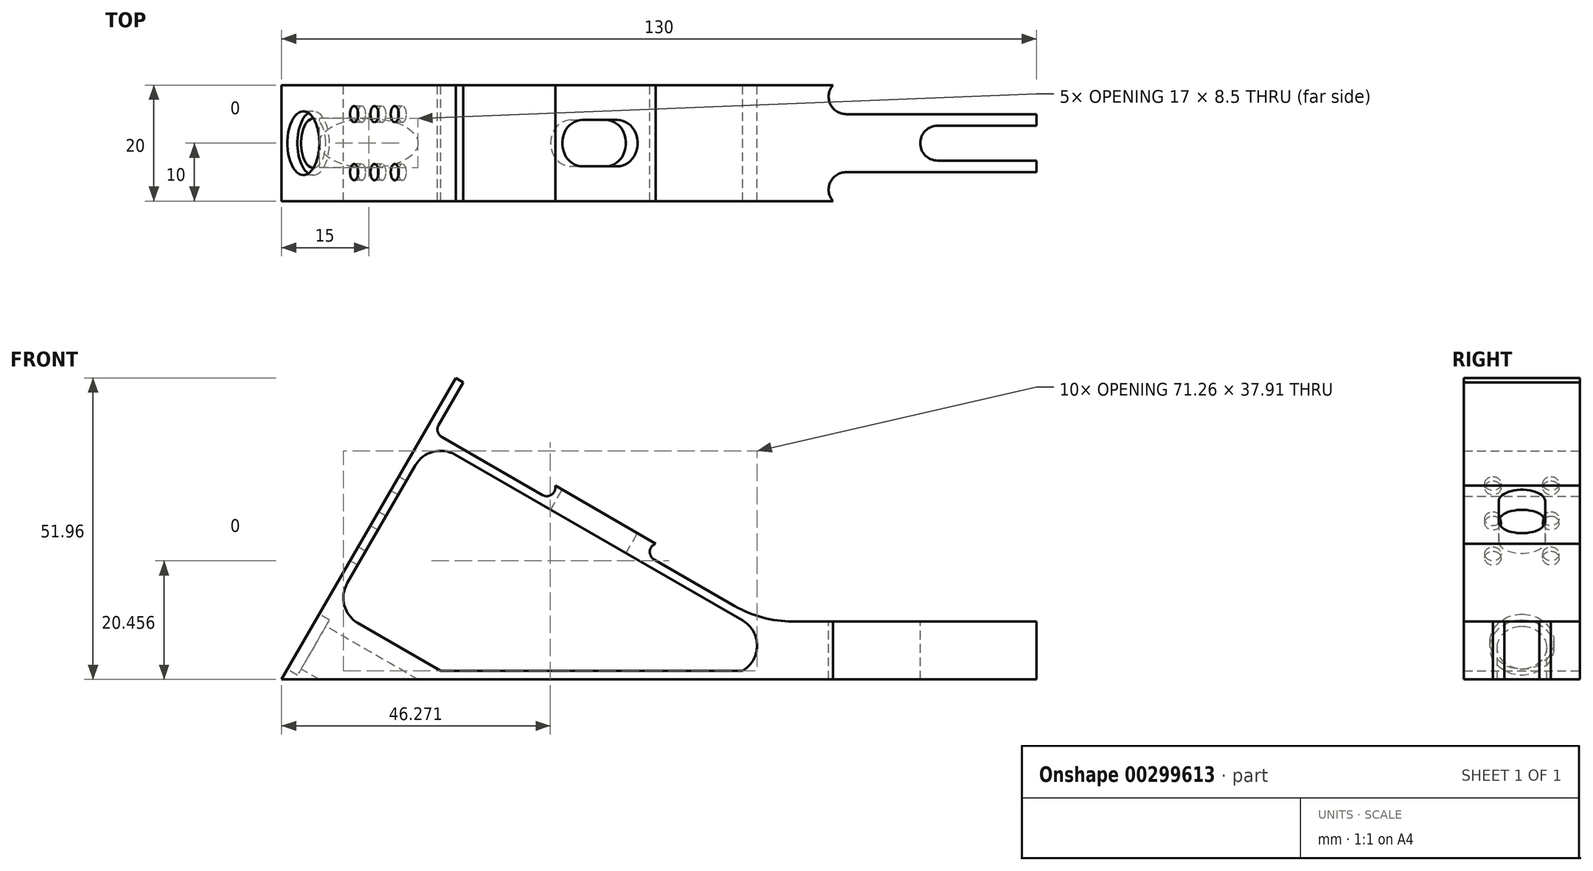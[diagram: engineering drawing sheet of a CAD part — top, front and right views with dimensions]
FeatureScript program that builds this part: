
annotation { "Feature Type Name" : "Feature", "Feature Type Description" : "" }
export const myFeature = defineFeature(function(context is Context, id is Id, definition is map)
    precondition{}
    {
        {
            var Q0;
            Q0=qCreatedBy(makeId("Front.planeOp"),FACE);
            var sketch = newSketch(context, id + "F0", { "sketchPlane" : qUnion([Q0])});
            skLineSegment(sketch, "E0", {"start": v(0, 0) * mm, "end": v(30, 51.96) * mm});
            skLineSegment(sketch, "E1", {"start": v(30, 51.96) * mm, "end": v(31.3, 51.21) * mm});
            skLineSegment(sketch, "E2", {"start": v(130, 10) * mm, "end": v(130, 0) * mm});
            skLineSegment(sketch, "E3", {"start": v(130, 0) * mm, "end": v(0, 0) * mm});
            skLineSegment(sketch, "E4", {"start": v(31.3, 51.21) * mm, "end": v(27.05, 43.85) * mm});
            skArc(sketch, "E5", {"start": v(27.05, 43.85) * mm, "mid": v(26.9, 42.71) * mm, "end": v(27.6, 41.8) * mm});
            skLineSegment(sketch, "E6", {"start": v(27.6, 41.8) * mm, "end": v(44.92, 31.8) * mm});
            skLineSegment(sketch, "E7", {"start": v(47.14, 33.4) * mm, "end": v(64.46, 23.4) * mm});
            skLineSegment(sketch, "E8", {"start": v(23.05, 36.92) * mm, "end": v(11.3, 16.57) * mm});
            skLineSegment(sketch, "E9", {"start": v(13.13, 9.74) * mm, "end": v(27.4, 1.5) * mm});
            skArc(sketch, "E10", {"start": v(29.88, 38.75) * mm, "mid": v(26.09, 39.25) * mm, "end": v(23.05, 36.92) * mm});
            skArc(sketch, "E11", {"start": v(11.3, 16.57) * mm, "mid": v(10.8, 12.78) * mm, "end": v(13.13, 9.74) * mm});
            skLineSegment(sketch, "E12", {"start": v(29.88, 38.75) * mm, "end": v(79.4, 10.16) * mm});
            skLineSegment(sketch, "E13", {"start": v(130, 10) * mm, "end": v(88.04, 10) * mm});
            skLineSegment(sketch, "E14", {"start": v(64.18, 20.68) * mm, "end": v(78.04, 12.68) * mm});
            skArc(sketch, "E15", {"start": v(78.04, 12.68) * mm, "mid": v(82.86, 10.68) * mm, "end": v(88.04, 10) * mm});
            skArc(sketch, "E16", {"start": v(79.4, 1.5) * mm, "mid": v(81.9, 5.83) * mm, "end": v(79.4, 10.16) * mm});
            skLineSegment(sketch, "E17", {"start": v(27.4, 1.5) * mm, "end": v(79.4, 1.5) * mm});
            skArc(sketch, "E18", {"start": v(44.92, 31.8) * mm, "mid": v(46.55, 31.89) * mm, "end": v(47.14, 33.4) * mm});
            skArc(sketch, "E19", {"start": v(64.46, 23.4) * mm, "mid": v(63.43, 22.14) * mm, "end": v(64.18, 20.68) * mm});
            skLineSegment(sketch, "E20", {"start": v(95, 10) * mm, "end": v(95, 0) * mm});
            skSolve(sketch);
        }
        {
            var Q0;
            Q0 = qSketchRegion(id + "F0", true);
            extrude(context, id + "F1", {"entities" : qUnion([Q0]), "endBound" : BoundingType.SYMMETRIC, "depth" : 20 * mm});
        }
        {
            var Q0;
            Q0=makeQuery(id+"F1.opExtrude","SWEPT_FACE",FACE,{"disambiguationData":[OSD([sQuery(id+"F0.wireOp",EDGE,"E7")])]});
            var sketch = newSketch(context, id + "F2", { "sketchPlane" : qUnion([Q0])});
            skPoint(sketch, "E21.startSnap0", {"position": v(24.12, 0) * mm});
            skPoint(sketch, "E21.endSnap0", {"position": v(24.12, 0) * mm});
            skLineSegment(sketch, "E22", {"start": v(29.5, 0) * mm, "end": v(36.5, 0) * mm, "construction": true});
            skArc(sketch, "E23.0.startCap", {"start": v(29.5, -4) * mm, "mid": v(25.5, 0) * mm, "end": v(29.5, 4) * mm});
            skArc(sketch, "E23.0.endCap", {"start": v(36.5, 4) * mm, "mid": v(40.5, 0) * mm, "end": v(36.5, -4) * mm});
            skLineSegment(sketch, "E23.0.left", {"start": v(29.5, 4) * mm, "end": v(36.5, 4) * mm});
            skLineSegment(sketch, "E23.0.right", {"start": v(29.5, -4) * mm, "end": v(36.5, -4) * mm});
            skSolve(sketch);
        }
        {
            var Q0;
            Q0 = qSketchRegion(id + "F2", true);
            extrude(context, id + "F3", {"entities" : qUnion([Q0]), "operationType" : NewBodyOperationType.REMOVE, "oppositeDirection" : true, "depth" : 4 * mm});
        }
        {
            var Q0;
            Q0=makeQuery(id+"F1.opExtrude","SWEPT_FACE",FACE,{"disambiguationData":[OSD([sQuery(id+"F0.wireOp",EDGE,"E0")])]});
            var sketch = newSketch(context, id + "F4", { "sketchPlane" : qUnion([Q0])});
            skPoint(sketch, "E24", {"position": v(0, 7.5) * mm});
            skCircle(sketch, "E25", {"center": v(0, 7.5) * mm, "radius": 5.5 * mm});
            skCircle(sketch, "E26", {"center": v(0, 7.5) * mm, "radius": 4.25 * mm});
            skLineSegment(sketch, "E27", {"start": v(0, 0) * mm, "end": v(0, 66.73) * mm, "construction": true});
            skPoint(sketch, "E28", {"position": v(-5, 25) * mm});
            skPoint(sketch, "E29", {"position": v(5, 25) * mm});
            skCircle(sketch, "E30", {"center": v(-5, 25) * mm, "radius": 1.4 * mm});
            skCircle(sketch, "E31", {"center": v(5, 25) * mm, "radius": 1.4 * mm});
            skPoint(sketch, "E32", {"position": v(-5, 32) * mm});
            skPoint(sketch, "E33", {"position": v(5, 32) * mm});
            skPoint(sketch, "E34", {"position": v(5, 39) * mm});
            skPoint(sketch, "E35", {"position": v(-5, 39) * mm});
            skCircle(sketch, "E36", {"center": v(-5, 32) * mm, "radius": 1.4 * mm});
            skCircle(sketch, "E37", {"center": v(5, 32) * mm, "radius": 1.4 * mm});
            skCircle(sketch, "E38", {"center": v(5, 39) * mm, "radius": 1.4 * mm});
            skCircle(sketch, "E39", {"center": v(-5, 39) * mm, "radius": 1.4 * mm});
            skSolve(sketch);
        }
        {
            var Q0;
            Q0=makeQuery(id+"F4.imprint","IMPRINT",FACE,{"disambiguationData":[TD([[makeQuery(id+"F4.imprint","IMPRINT",EDGE,{"derivedFrom":sQuery(id+"F4.wireOp",EDGE,"E39")}),1.0]])]});
            var Q1;
            Q1=makeQuery(id+"F4.imprint","IMPRINT",FACE,{"disambiguationData":[TD([[makeQuery(id+"F4.imprint","IMPRINT",EDGE,{"derivedFrom":sQuery(id+"F4.wireOp",EDGE,"E36")}),1.0]])]});
            var Q2;
            Q2=makeQuery(id+"F4.imprint","IMPRINT",FACE,{"disambiguationData":[TD([[makeQuery(id+"F4.imprint","IMPRINT",EDGE,{"derivedFrom":sQuery(id+"F4.wireOp",EDGE,"E31")}),1.0]])]});
            var Q3;
            Q3=makeQuery(id+"F4.imprint","IMPRINT",FACE,{"disambiguationData":[TD([[makeQuery(id+"F4.imprint","IMPRINT",EDGE,{"derivedFrom":sQuery(id+"F4.wireOp",EDGE,"E37")}),1.0]])]});
            var Q4;
            Q4=makeQuery(id+"F4.imprint","IMPRINT",FACE,{"disambiguationData":[TD([[makeQuery(id+"F4.imprint","IMPRINT",EDGE,{"derivedFrom":sQuery(id+"F4.wireOp",EDGE,"E38")}),1.0]])]});
            var Q5;
            Q5=makeQuery(id+"F4.imprint","IMPRINT",FACE,{"disambiguationData":[TD([[makeQuery(id+"F4.imprint","IMPRINT",EDGE,{"derivedFrom":sQuery(id+"F4.wireOp",EDGE,"E30")}),1.0]])]});
            extrude(context, id + "F5", {"entities" : qUnion([Q0, Q1, Q2, Q3, Q4, Q5]), "operationType" : NewBodyOperationType.REMOVE, "oppositeDirection" : true, "depth" : 1.5 * mm});
        }
        {
            var Q0;
            Q0=makeQuery(id+"F4.imprint","IMPRINT",FACE,{"disambiguationData":[TD([[makeQuery(id+"F4.imprint","IMPRINT",EDGE,{"derivedFrom":sQuery(id+"F4.wireOp",EDGE,"E25")}),1.0]])]});
            extrude(context, id + "F6", {"entities" : qUnion([Q0]), "operationType" : NewBodyOperationType.REMOVE, "oppositeDirection" : true, "depth" : 2 * mm});
        }
        {
            var Q0;
            Q0=makeQuery(id+"F6.boolean.opBoolean","SPLIT",FACE,{"disambiguationData":[TD([makeQuery(id+"F6.opExtrude","SWEPT_FACE",FACE,{"disambiguationData":[OSD([sQuery(id+"F4.wireOp",EDGE,"E26")])]})])],"derivedFrom":makeQuery(id+"F1.opExtrude","SWEPT_FACE",FACE,{"disambiguationData":[OSD([sQuery(id+"F0.wireOp",EDGE,"E0")])]})});
            extrude(context, id + "F7", {"entities" : qUnion([Q0]), "operationType" : NewBodyOperationType.REMOVE, "endBound" : BoundingType.THROUGH_ALL, "oppositeDirection" : true, "depth" : 25 * mm});
        }
        {
            var Q0;
            Q0=makeQuery(id+"F1.opExtrude","SWEPT_FACE",FACE,{"disambiguationData":[OSD([sQuery(id+"F0.wireOp",EDGE,"E13")])]});
            var sketch = newSketch(context, id + "F8", { "sketchPlane" : qUnion([Q0])});
            skLineSegment(sketch, "E40", {"start": v(88.04, 0) * mm, "end": v(132.2, 0) * mm, "construction": true});
            skPoint(sketch, "E40.endSnap0", {"position": v(130, 0) * mm});
            skLineSegment(sketch, "E41", {"start": v(130, 5) * mm, "end": v(97.24, 5) * mm});
            skLineSegment(sketch, "E42", {"start": v(130, -5) * mm, "end": v(97.24, -5) * mm});
            skLineSegment(sketch, "E43", {"start": v(113, 3) * mm, "end": v(130, 3) * mm});
            skLineSegment(sketch, "E44", {"start": v(113, -3) * mm, "end": v(130, -3) * mm});
            skLineSegment(sketch, "E45", {"start": v(130, 5) * mm, "end": v(130, 3) * mm});
            skLineSegment(sketch, "E46", {"start": v(130, -3) * mm, "end": v(130, -5) * mm});
            skLineSegment(sketch, "E47", {"start": v(130, 10) * mm, "end": v(95, 10) * mm});
            skLineSegment(sketch, "E48", {"start": v(130, 10) * mm, "end": v(130, -10) * mm});
            skLineSegment(sketch, "E49", {"start": v(95, -10) * mm, "end": v(130, -10) * mm});
            skPoint(sketch, "E50", {"position": v(113, 0) * mm});
            skArc(sketch, "E51", {"start": v(95, 10) * mm, "mid": v(94.5, 6.78) * mm, "end": v(97.24, 5) * mm});
            skArc(sketch, "E52", {"start": v(97.24, -5) * mm, "mid": v(94.5, -6.78) * mm, "end": v(95, -10) * mm});
            skLineSegment(sketch, "E53", {"start": v(95, 10) * mm, "end": v(130, 10) * mm});
            skLineSegment(sketch, "E54", {"start": v(130, 10) * mm, "end": v(130, 5) * mm});
            skLineSegment(sketch, "E55", {"start": v(130, -5) * mm, "end": v(130, -10) * mm});
            skArc(sketch, "E56", {"start": v(113, 3) * mm, "mid": v(110, 0) * mm, "end": v(113, -3) * mm});
            skSolve(sketch);
        }
        {
            var Q0;
            Q0 = qSketchRegion(id + "F8", true);
            extrude(context, id + "F9", {"entities" : qUnion([Q0]), "operationType" : NewBodyOperationType.REMOVE, "endBound" : BoundingType.THROUGH_ALL, "oppositeDirection" : true, "depth" : 25 * mm});
        }
    });
